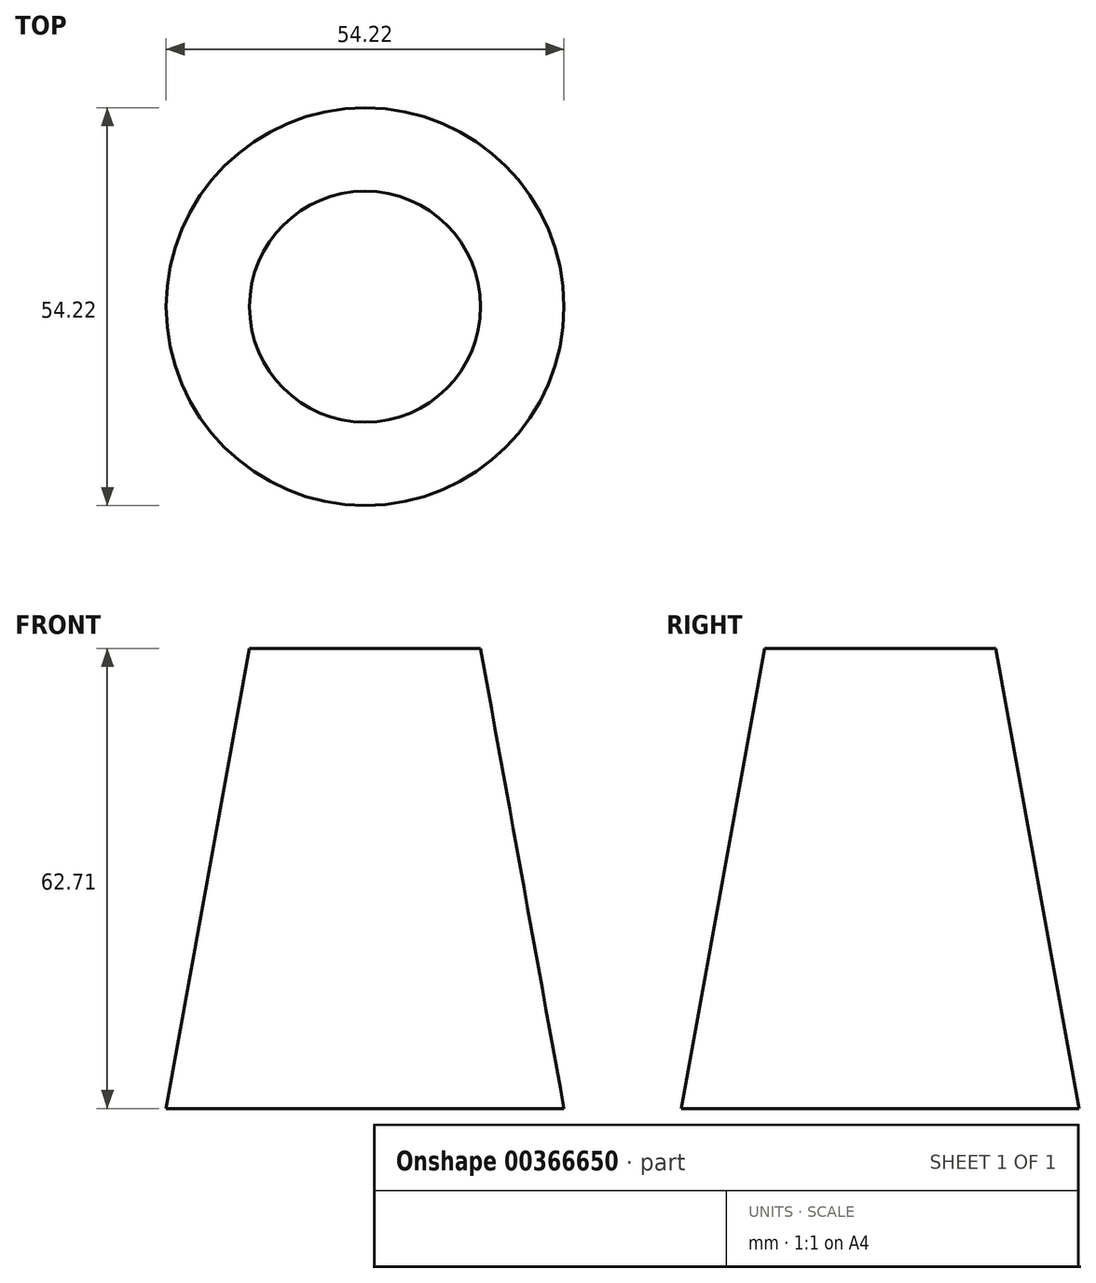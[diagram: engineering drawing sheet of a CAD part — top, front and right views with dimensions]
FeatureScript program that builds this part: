
annotation { "Feature Type Name" : "Feature", "Feature Type Description" : "" }
export const myFeature = defineFeature(function(context is Context, id is Id, definition is map)
    precondition{}
    {
        {
            var Q0;
            Q0=qCreatedBy(makeId("Front.planeOp"),FACE);
            var sketch = newSketch(context, id + "F0", { "sketchPlane" : qUnion([Q0])});
            skPoint(sketch, "E0.0.midPoint", {"position": v(23.16, -37.24) * mm});
            skPoint(sketch, "E1.0.midPoint", {"position": v(10.68, 25.23) * mm});
            skPoint(sketch, "E2.0.midPoint", {"position": v(16.78, -5.45) * mm});
            skLineSegment(sketch, "E3", {"start": v(0, -72) * mm, "end": v(0, 68.85) * mm, "construction": true});
            skLineSegment(sketch, "E4", {"start": v(0, -56.23) * mm, "end": v(27.11, -56.23) * mm});
            skLineSegment(sketch, "E5", {"start": v(27.11, -56.23) * mm, "end": v(15.75, 6.48) * mm});
            skLineSegment(sketch, "E6", {"start": v(15.75, 6.48) * mm, "end": v(0, 6.48) * mm});
            skSolve(sketch);
        }
        {
            var Q0;
            Q0=sQuery(id+"F0.wireOp",EDGE,"E4");
            var Q1;
            Q1=sQuery(id+"F0.wireOp",EDGE,"E5");
            var Q2;
            Q2=sQuery(id+"F0.wireOp",EDGE,"E3");
            revolve(context, id + "F1", {"bodyType" : ToolBodyType.SURFACE, "surfaceEntities" : qUnion([Q0, Q1]), "axis" : qUnion([Q2]), "revolveType" : RevolveType.FULL});
        }
    });
